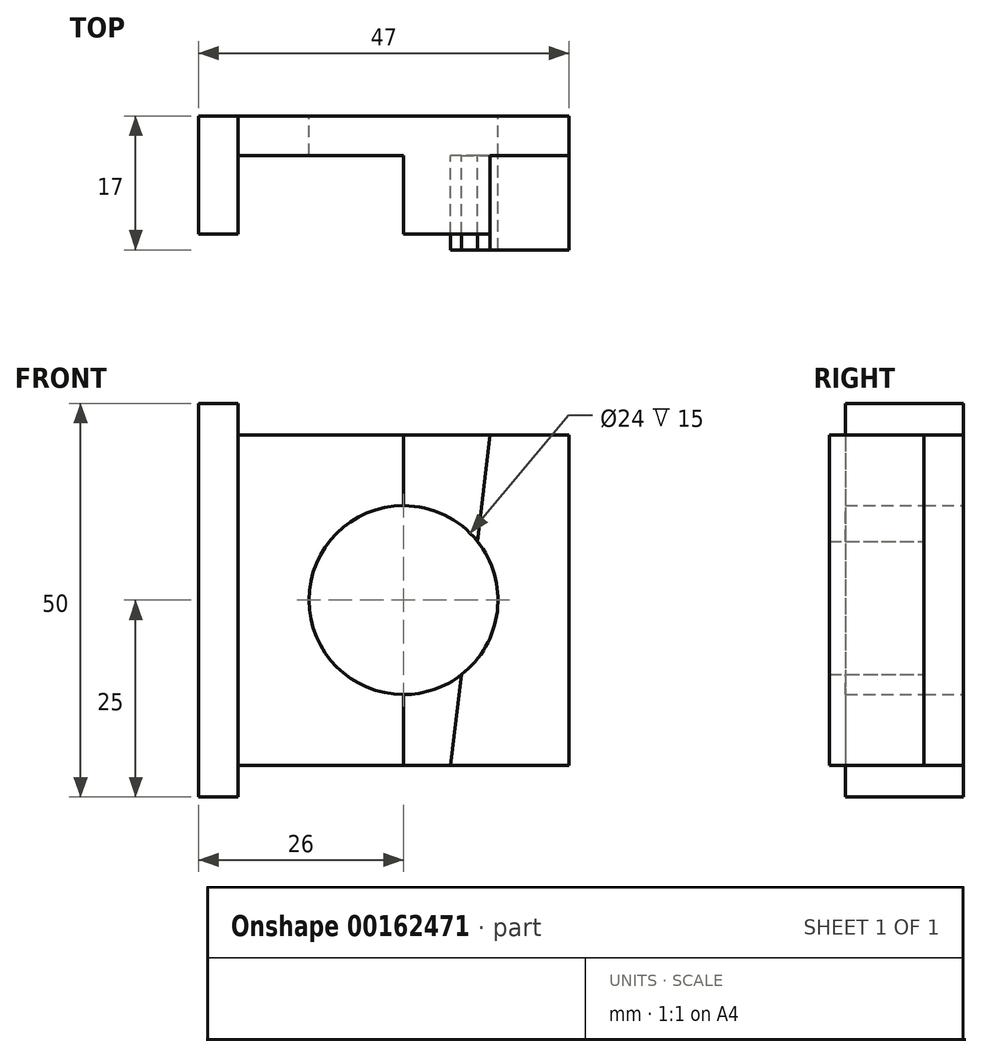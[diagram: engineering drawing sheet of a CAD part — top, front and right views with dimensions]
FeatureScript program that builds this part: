
annotation { "Feature Type Name" : "Feature", "Feature Type Description" : "" }
export const myFeature = defineFeature(function(context is Context, id is Id, definition is map)
    precondition{}
    {
        {
            var Q0;
            Q0=qCreatedBy(makeId("Front.planeOp"),FACE);
            var sketch = newSketch(context, id + "F0", { "sketchPlane" : qUnion([Q0])});
            skLineSegment(sketch, "E0.bottom", {"start": v(21, 21) * mm, "end": v(-21, 21) * mm});
            skLineSegment(sketch, "E0.top", {"start": v(21, -21) * mm, "end": v(-21, -21) * mm});
            skLineSegment(sketch, "E0.left", {"start": v(21, 21) * mm, "end": v(21, -21) * mm});
            skLineSegment(sketch, "E0.right", {"start": v(-21, 21) * mm, "end": v(-21, -21) * mm});
            skPoint(sketch, "E0.middle", {"position": v(0, 0) * mm});
            skCircle(sketch, "E1", {"center": v(0, 0) * mm, "radius": 12 * mm});
            skSolve(sketch);
        }
        {
            var Q0;
            Q0 = qSketchRegion(id + "F0", true);
            extrude(context, id + "F1", {"entities" : qUnion([Q0]), "depth" : 5 * mm});
        }
        {
            var Q0;
            Q0=makeQuery(id+"F1.opExtrude","SWEPT_FACE",FACE,{"disambiguationData":[OSD([sQuery(id+"F0.wireOp",EDGE,"E0.right")])]});
            var sketch = newSketch(context, id + "F2", { "sketchPlane" : qUnion([Q0])});
            skLineSegment(sketch, "E2.bottom", {"start": v(0, 25) * mm, "end": v(15, 25) * mm});
            skLineSegment(sketch, "E2.top", {"start": v(0, -25) * mm, "end": v(15, -25) * mm});
            skLineSegment(sketch, "E2.left", {"start": v(0, 25) * mm, "end": v(0, -25) * mm});
            skLineSegment(sketch, "E2.right", {"start": v(15, 25) * mm, "end": v(15, -25) * mm});
            skPoint(sketch, "E2.middle", {"position": v(7.5, 0) * mm});
            skPoint(sketch, "E2.middle.positionSnap0", {"position": v(5, 0) * mm});
            skPoint(sketch, "E2.centerSnap0", {"position": v(5, 0) * mm});
            skSolve(sketch);
        }
        {
            var Q0;
            Q0 = qSketchRegion(id + "F2", true);
            extrude(context, id + "F3", {"entities" : qUnion([Q0]), "operationType" : NewBodyOperationType.ADD, "depth" : 5 * mm});
        }
        {
            var Q0;
            Q0=makeQuery(id+"F1.opExtrude","CAP_FACE",FACE,{"disambiguationData":[OSD([sQuery(id+"F0.wireOp",EDGE,"E0.bottom"),sQuery(id+"F0.wireOp",EDGE,"E0.top"),sQuery(id+"F0.wireOp",EDGE,"E0.left"),sQuery(id+"F0.wireOp",EDGE,"E0.right"),sQuery(id+"F0.wireOp",EDGE,"E1")])],"isStart":false});
            var sketch = newSketch(context, id + "F4", { "sketchPlane" : qUnion([Q0])});
            skLineSegment(sketch, "E3", {"start": v(11, 21) * mm, "end": v(6, -21) * mm});
            skLineSegment(sketch, "E4", {"start": v(0, 21) * mm, "end": v(0, -21) * mm});
            skSolve(sketch);
        }
        {
            var Q0;
            Q0 = qSketchRegion(id + "F4", true);
            var Q1;
            {var subQ0=sQuery(id+"F4.wireOp",EDGE,"E3");var subQ1=makeQuery(id+"F1.opExtrude","CAP_EDGE",EDGE,{"disambiguationData":[OSD([sQuery(id+"F0.wireOp",EDGE,"E0.bottom")])],"isStart":false});var subQ2=makeQuery(id+"F4.imprint","INTERSECT",VERTEX,{"derivedFrom":[subQ1,subQ0]});Q1=makeQuery(id+"F4.imprint","IMPRINT",FACE,{"disambiguationData":[TD([[makeQuery(id+"F4.imprint","IMPRINT",EDGE,{"disambiguationData":[TD([[subQ2,-1.0]])],"derivedFrom":subQ0}),-1.0]])]});}
            var Q2;
            {var subQ0=sQuery(id+"F4.wireOp",EDGE,"E3");var subQ1=makeQuery(id+"F1.opExtrude","CAP_EDGE",EDGE,{"disambiguationData":[OSD([sQuery(id+"F0.wireOp",EDGE,"E0.top")])],"isStart":false});var subQ2=makeQuery(id+"F4.imprint","INTERSECT",VERTEX,{"derivedFrom":[subQ1,subQ0]});Q2=makeQuery(id+"F4.imprint","IMPRINT",FACE,{"disambiguationData":[TD([[makeQuery(id+"F4.imprint","IMPRINT",EDGE,{"disambiguationData":[TD([[subQ2,1.0]])],"derivedFrom":subQ0}),-1.0]])]});}
            extrude(context, id + "F5", {"entities" : qUnion([Q0, Q1, Q2]), "operationType" : NewBodyOperationType.ADD, "depth" : 10 * mm});
        }
        {
            var Q0;
            {var subQ0=sQuery(id+"F0.wireOp",EDGE,"E1");var subQ2=sQuery(id+"F0.wireOp",EDGE,"E0.bottom");var subQ6=sQuery(id+"F0.wireOp",EDGE,"E0.left");var subQ7=sQuery(id+"F0.wireOp",EDGE,"E0.top");Q0=makeQuery(id+"F5.boolean.opBoolean","SPLIT",FACE,{"disambiguationData":[TD([makeQuery(id+"F1.opExtrude","SWEPT_FACE",FACE,{"disambiguationData":[OSD([subQ6])]})])],"derivedFrom":makeQuery(id+"F1.opExtrude","CAP_FACE",FACE,{"disambiguationData":[OSD([subQ2,subQ7,subQ6,sQuery(id+"F0.wireOp",EDGE,"E0.right"),subQ0])],"isStart":false})});}
            extrude(context, id + "F6", {"entities" : qUnion([Q0]), "depth" : 12 * mm});
        }
    });
